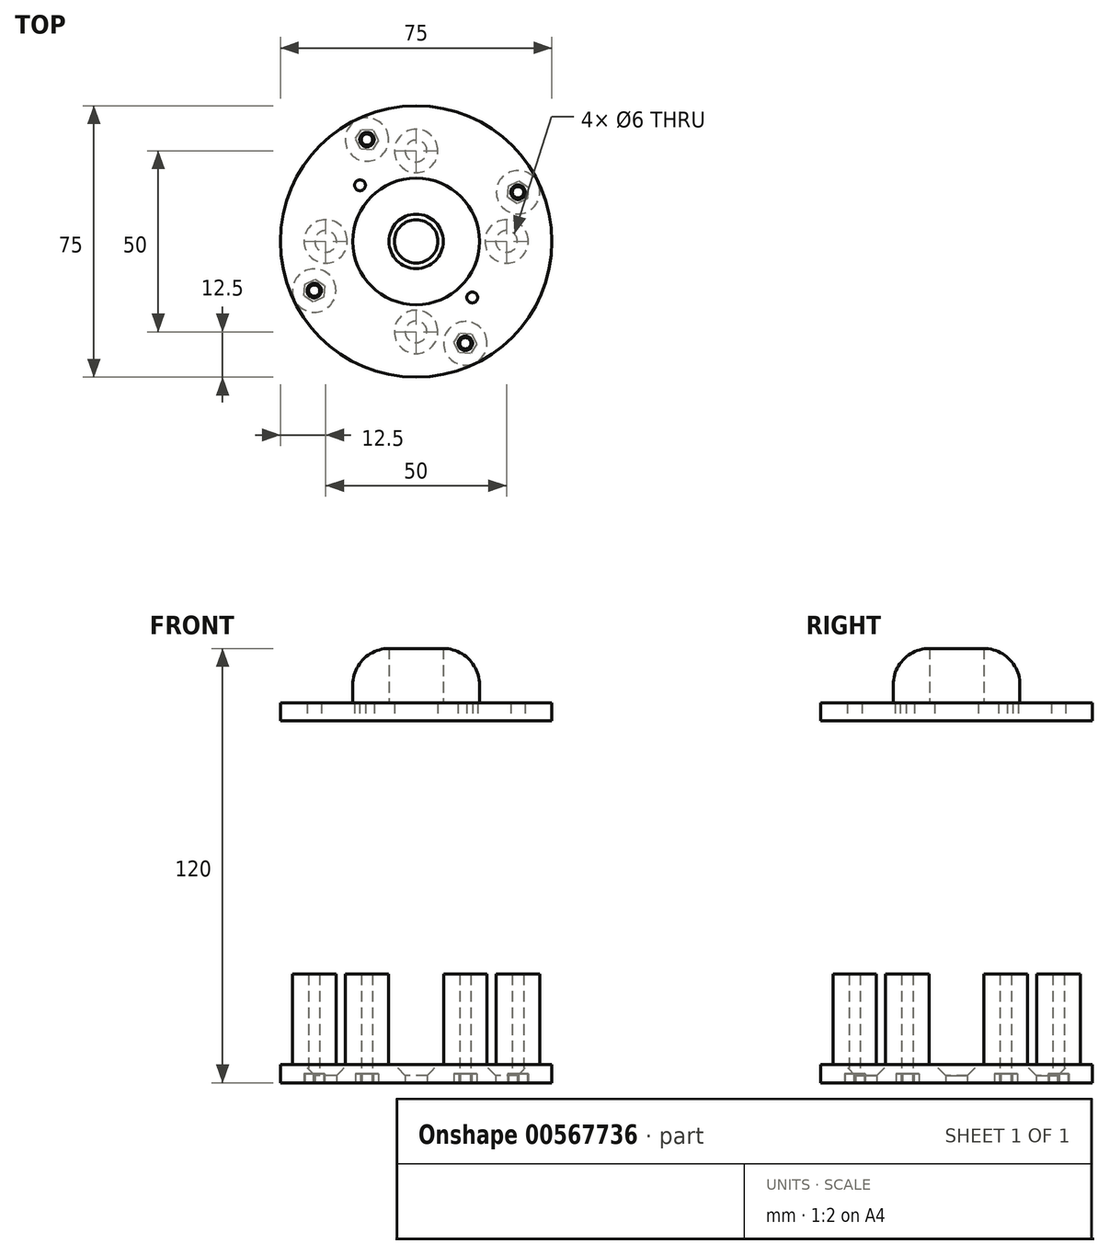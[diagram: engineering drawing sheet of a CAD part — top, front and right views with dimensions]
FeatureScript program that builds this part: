
annotation { "Feature Type Name" : "Feature", "Feature Type Description" : "" }
export const myFeature = defineFeature(function(context is Context, id is Id, definition is map)
    precondition{}
    {
        {
            var Q0;
            Q0=qCreatedBy(makeId("Top.planeOp"),FACE);
            var sketch = newSketch(context, id + "F0", { "sketchPlane" : qUnion([Q0])});
            skCircle(sketch, "E0", {"center": v(0, 0) * mm, "radius": 37.5 * mm});
            skCircle(sketch, "E1", {"center": v(0, 25) * mm, "radius": 3 * mm});
            skCircle(sketch, "E2.1.0", {"center": v(-25, 0) * mm, "radius": 3 * mm});
            skCircle(sketch, "E2.2.0", {"center": v(0, -25) * mm, "radius": 3 * mm});
            skCircle(sketch, "E2.3.0", {"center": v(25, 0) * mm, "radius": 3 * mm});
            skCircle(sketch, "E3.cCircle", {"center": v(28.15, 13.59) * mm, "radius": 2.75 * mm, "construction": true});
            skLineSegment(sketch, "E3.0", {"start": v(30.78, 11.8) * mm, "end": v(27.92, 10.42) * mm});
            skLineSegment(sketch, "E3.1", {"start": v(27.92, 10.42) * mm, "end": v(25.3, 12.2) * mm});
            skLineSegment(sketch, "E3.2", {"start": v(25.3, 12.2) * mm, "end": v(25.52, 15.38) * mm});
            skLineSegment(sketch, "E3.3", {"start": v(25.52, 15.38) * mm, "end": v(28.38, 16.76) * mm});
            skLineSegment(sketch, "E3.4", {"start": v(28.38, 16.76) * mm, "end": v(31, 14.97) * mm});
            skLineSegment(sketch, "E3.5", {"start": v(31, 14.97) * mm, "end": v(30.78, 11.8) * mm});
            skPoint(sketch, "E3.0.midPoint", {"position": v(29.35, 11.11) * mm});
            skLineSegment(sketch, "E4", {"start": v(0, 0) * mm, "end": v(0, 57.37) * mm, "construction": true});
            skLineSegment(sketch, "E5", {"start": v(0, 0) * mm, "end": v(83.24, 0) * mm, "construction": true});
            skLineSegment(sketch, "E6", {"start": v(0, 0) * mm, "end": v(43.66, 21.08) * mm, "construction": true});
            skLineSegment(sketch, "E7.1.0", {"start": v(-16.76, 28.38) * mm, "end": v(-14.97, 31) * mm});
            skLineSegment(sketch, "E7.1.1", {"start": v(-15.38, 25.52) * mm, "end": v(-16.76, 28.38) * mm});
            skLineSegment(sketch, "E7.1.2", {"start": v(-12.2, 25.3) * mm, "end": v(-15.38, 25.52) * mm});
            skLineSegment(sketch, "E7.1.3", {"start": v(-10.42, 27.92) * mm, "end": v(-12.2, 25.3) * mm});
            skLineSegment(sketch, "E7.1.4", {"start": v(-11.8, 30.78) * mm, "end": v(-10.42, 27.92) * mm});
            skLineSegment(sketch, "E7.1.5", {"start": v(-14.97, 31) * mm, "end": v(-11.8, 30.78) * mm});
            skLineSegment(sketch, "E7.2.0", {"start": v(-28.38, -16.76) * mm, "end": v(-31, -14.97) * mm});
            skLineSegment(sketch, "E7.2.1", {"start": v(-25.52, -15.38) * mm, "end": v(-28.38, -16.76) * mm});
            skLineSegment(sketch, "E7.2.2", {"start": v(-25.3, -12.2) * mm, "end": v(-25.52, -15.38) * mm});
            skLineSegment(sketch, "E7.2.3", {"start": v(-27.92, -10.42) * mm, "end": v(-25.3, -12.2) * mm});
            skLineSegment(sketch, "E7.2.4", {"start": v(-30.78, -11.8) * mm, "end": v(-27.92, -10.42) * mm});
            skLineSegment(sketch, "E7.2.5", {"start": v(-31, -14.97) * mm, "end": v(-30.78, -11.8) * mm});
            skLineSegment(sketch, "E7.3.0", {"start": v(16.76, -28.38) * mm, "end": v(14.97, -31) * mm});
            skLineSegment(sketch, "E7.3.1", {"start": v(15.38, -25.52) * mm, "end": v(16.76, -28.38) * mm});
            skLineSegment(sketch, "E7.3.2", {"start": v(12.2, -25.3) * mm, "end": v(15.38, -25.52) * mm});
            skLineSegment(sketch, "E7.3.3", {"start": v(10.42, -27.92) * mm, "end": v(12.2, -25.3) * mm});
            skLineSegment(sketch, "E7.3.4", {"start": v(11.8, -30.78) * mm, "end": v(10.42, -27.92) * mm});
            skLineSegment(sketch, "E7.3.5", {"start": v(14.97, -31) * mm, "end": v(11.8, -30.78) * mm});
            skCircle(sketch, "E8", {"center": v(28.15, 13.59) * mm, "radius": 1.55 * mm});
            skCircle(sketch, "E9.1.0", {"center": v(-13.59, 28.15) * mm, "radius": 1.55 * mm});
            skCircle(sketch, "E9.2.0", {"center": v(-28.15, -13.59) * mm, "radius": 1.55 * mm});
            skCircle(sketch, "E9.3.0", {"center": v(13.59, -28.15) * mm, "radius": 1.55 * mm});
            skLineSegment(sketch, "E10.bottom", {"start": v(-21.15, -21.15) * mm, "end": v(21.15, -21.15) * mm, "construction": true});
            skLineSegment(sketch, "E10.top", {"start": v(-21.15, 21.15) * mm, "end": v(21.15, 21.15) * mm, "construction": true});
            skLineSegment(sketch, "E10.left", {"start": v(-21.15, -21.15) * mm, "end": v(-21.15, 21.15) * mm, "construction": true});
            skLineSegment(sketch, "E10.right", {"start": v(21.15, -21.15) * mm, "end": v(21.15, 21.15) * mm, "construction": true});
            skCircle(sketch, "E11", {"center": v(28.15, 13.59) * mm, "radius": 6 * mm});
            skCircle(sketch, "E12.1.0", {"center": v(-13.59, 28.15) * mm, "radius": 6 * mm});
            skCircle(sketch, "E12.2.0", {"center": v(-28.15, -13.59) * mm, "radius": 6 * mm});
            skCircle(sketch, "E12.3.0", {"center": v(13.59, -28.15) * mm, "radius": 6 * mm});
            skSolve(sketch);
        }
        {
            var Q0;
            Q0=makeQuery(id+"F0.imprint","IMPRINT",FACE,{"disambiguationData":[TD([[makeQuery(id+"F0.imprint","IMPRINT",EDGE,{"derivedFrom":sQuery(id+"F0.wireOp",EDGE,"E0")}),1.0]])]});
            var Q1;
            Q1=makeQuery(id+"F0.imprint","IMPRINT",FACE,{"disambiguationData":[TD([[makeQuery(id+"F0.imprint","IMPRINT",EDGE,{"derivedFrom":sQuery(id+"F0.wireOp",EDGE,"E7.1.0")}),-1.0]])]});
            var Q2;
            Q2=makeQuery(id+"F0.imprint","IMPRINT",FACE,{"disambiguationData":[TD([[makeQuery(id+"F0.imprint","IMPRINT",EDGE,{"derivedFrom":sQuery(id+"F0.wireOp",EDGE,"E7.3.0")}),-1.0]])]});
            var Q3;
            Q3=makeQuery(id+"F0.imprint","IMPRINT",FACE,{"disambiguationData":[TD([[makeQuery(id+"F0.imprint","IMPRINT",EDGE,{"derivedFrom":sQuery(id+"F0.wireOp",EDGE,"E7.2.0")}),-1.0]])]});
            var Q4;
            Q4=makeQuery(id+"F0.imprint","IMPRINT",FACE,{"disambiguationData":[TD([[makeQuery(id+"F0.imprint","IMPRINT",EDGE,{"derivedFrom":sQuery(id+"F0.wireOp",EDGE,"E3.0")}),1.0]])]});
            var Q5;
            Q5=makeQuery(id+"F0.imprint","IMPRINT",FACE,{"disambiguationData":[TD([[makeQuery(id+"F0.imprint","IMPRINT",EDGE,{"derivedFrom":sQuery(id+"F0.wireOp",EDGE,"E3.0")}),-1.0]])]});
            var Q6;
            Q6=makeQuery(id+"F0.imprint","IMPRINT",FACE,{"disambiguationData":[TD([[makeQuery(id+"F0.imprint","IMPRINT",EDGE,{"derivedFrom":sQuery(id+"F0.wireOp",EDGE,"E7.2.0")}),1.0]])]});
            var Q7;
            Q7=makeQuery(id+"F0.imprint","IMPRINT",FACE,{"disambiguationData":[TD([[makeQuery(id+"F0.imprint","IMPRINT",EDGE,{"derivedFrom":sQuery(id+"F0.wireOp",EDGE,"E7.1.0")}),1.0]])]});
            var Q8;
            Q8=makeQuery(id+"F0.imprint","IMPRINT",FACE,{"disambiguationData":[TD([[makeQuery(id+"F0.imprint","IMPRINT",EDGE,{"derivedFrom":sQuery(id+"F0.wireOp",EDGE,"E7.3.0")}),1.0]])]});
            extrude(context, id + "F1", {"entities" : qUnion([Q0, Q1, Q2, Q3, Q4, Q5, Q6, Q7, Q8]), "depth" : 5 * mm, "offsetDistance" : 25 * mm});
        }
        {
            var Q0;
            Q0=makeQuery(id+"F1.opExtrude","CAP_EDGE",EDGE,{"disambiguationData":[OSD([sQuery(id+"F0.wireOp",EDGE,"E1")])],"isStart":false});
            var Q1;
            Q1=makeQuery(id+"F1.opExtrude","CAP_EDGE",EDGE,{"disambiguationData":[OSD([sQuery(id+"F0.wireOp",EDGE,"E2.3.0")])],"isStart":false});
            var Q2;
            Q2=makeQuery(id+"F1.opExtrude","CAP_EDGE",EDGE,{"disambiguationData":[OSD([sQuery(id+"F0.wireOp",EDGE,"E2.2.0")])],"isStart":false});
            var Q3;
            Q3=makeQuery(id+"F1.opExtrude","CAP_EDGE",EDGE,{"disambiguationData":[OSD([sQuery(id+"F0.wireOp",EDGE,"E2.1.0")])],"isStart":false});
            chamfer(context, id + "F2", {"entities" : qUnion([Q0, Q1, Q2, Q3]), "width" : 3 * mm, "tangentPropagation" : true});
        }
        {
            var Q0;
            Q0=qCreatedBy(makeId("Top.planeOp"),FACE);
            cPlane(context, id + "F3", {"entities" : qUnion([Q0]), "cplaneType" : CPlaneType.OFFSET, "offset" : 100 * mm, "width" : 150 * mm, "height" : 150 * mm});
        }
        {
            var Q0;
            Q0=qCreatedBy(id+"F3.planeOp",FACE);
            var sketch = newSketch(context, id + "F4", { "sketchPlane" : qUnion([Q0])});
            skCircle(sketch, "E13", {"center": v(0, 0) * mm, "radius": 37.5 * mm});
            skCircle(sketch, "E14", {"center": v(28.15, 13.59) * mm, "radius": 2 * mm});
            skCircle(sketch, "E15.1.0", {"center": v(-13.59, 28.15) * mm, "radius": 2 * mm});
            skCircle(sketch, "E15.2.0", {"center": v(-28.15, -13.59) * mm, "radius": 2 * mm});
            skCircle(sketch, "E15.3.0", {"center": v(13.59, -28.15) * mm, "radius": 2 * mm});
            skLineSegment(sketch, "E16.bottom", {"start": v(21.15, 21.15) * mm, "end": v(-21.15, 21.15) * mm, "construction": true});
            skLineSegment(sketch, "E16.top", {"start": v(21.15, -21.15) * mm, "end": v(-21.15, -21.15) * mm, "construction": true});
            skLineSegment(sketch, "E16.left", {"start": v(21.15, 21.15) * mm, "end": v(21.15, -21.15) * mm, "construction": true});
            skLineSegment(sketch, "E16.right", {"start": v(-21.15, 21.15) * mm, "end": v(-21.15, -21.15) * mm, "construction": true});
            skLineSegment(sketch, "E17", {"start": v(0, 0) * mm, "end": v(0, -15.5) * mm});
            skLineSegment(sketch, "E18", {"start": v(0, -15.5) * mm, "end": v(15.5, -15.5) * mm});
            skCircle(sketch, "E19", {"center": v(15.5, -15.5) * mm, "radius": 1.5 * mm});
            skCircle(sketch, "E20.MirrorC", {"center": v(-15.5, -15.5) * mm, "radius": 1.5 * mm});
            skLineSegment(sketch, "E21", {"start": v(0, 0) * mm, "end": v(8.71, 0) * mm, "construction": true});
            skCircle(sketch, "E22.MirrorC", {"center": v(-15.5, 15.5) * mm, "radius": 1.5 * mm});
            skCircle(sketch, "E23.MirrorC", {"center": v(15.5, 15.5) * mm, "radius": 1.5 * mm});
            skCircle(sketch, "E24", {"center": v(0, 0) * mm, "radius": 6 * mm});
            skSolve(sketch);
        }
        {
            var Q0;
            Q0=makeQuery(id+"F4.imprint","IMPRINT",FACE,{"disambiguationData":[TD([[makeQuery(id+"F4.imprint","IMPRINT",EDGE,{"derivedFrom":sQuery(id+"F4.wireOp",EDGE,"E13")}),1.0]])]});
            var Q1;
            Q1=makeQuery(id+"F4.imprint","IMPRINT",FACE,{"disambiguationData":[TD([[makeQuery(id+"F4.imprint","IMPRINT",EDGE,{"derivedFrom":sQuery(id+"F4.wireOp",EDGE,"E19")}),-1.0]])]});
            extrude(context, id + "F5", {"entities" : qUnion([Q0, Q1]), "depth" : 5 * mm, "offsetDistance" : 25 * mm});
        }
        {
            var Q0;
            Q0=makeQuery(id+"F4.imprint","IMPRINT",FACE,{"disambiguationData":[TD([[makeQuery(id+"F4.imprint","IMPRINT",EDGE,{"derivedFrom":sQuery(id+"F4.wireOp",EDGE,"E19")}),-1.0]])]});
            var Q1;
            Q1=makeQuery(id+"F4.imprint","IMPRINT",FACE,{"disambiguationData":[TD([[makeQuery(id+"F4.imprint","IMPRINT",EDGE,{"derivedFrom":sQuery(id+"F4.wireOp",EDGE,"E20.MirrorC")}),1.0]])]});
            var Q2;
            Q2=makeQuery(id+"F4.imprint","IMPRINT",FACE,{"disambiguationData":[TD([[makeQuery(id+"F4.imprint","IMPRINT",EDGE,{"derivedFrom":sQuery(id+"F4.wireOp",EDGE,"E22.MirrorC")}),-1.0]])]});
            var Q3;
            Q3=makeQuery(id+"F4.imprint","IMPRINT",FACE,{"disambiguationData":[TD([[makeQuery(id+"F4.imprint","IMPRINT",EDGE,{"derivedFrom":sQuery(id+"F4.wireOp",EDGE,"E23.MirrorC")}),1.0]])]});
            extrude(context, id + "F6", {"entities" : qUnion([Q0, Q1, Q2, Q3]), "depth" : 5 * mm, "offsetDistance" : 25 * mm});
        }
        {
            var Q0;
            Q0=makeQuery(id+"F0.imprint","IMPRINT",FACE,{"disambiguationData":[TD([[makeQuery(id+"F0.imprint","IMPRINT",EDGE,{"derivedFrom":sQuery(id+"F0.wireOp",EDGE,"E3.0")}),1.0]])]});
            var Q1;
            Q1=makeQuery(id+"F0.imprint","IMPRINT",FACE,{"disambiguationData":[TD([[makeQuery(id+"F0.imprint","IMPRINT",EDGE,{"derivedFrom":sQuery(id+"F0.wireOp",EDGE,"E3.0")}),-1.0]])]});
            var Q2;
            Q2=makeQuery(id+"F0.imprint","IMPRINT",FACE,{"disambiguationData":[TD([[makeQuery(id+"F0.imprint","IMPRINT",EDGE,{"derivedFrom":sQuery(id+"F0.wireOp",EDGE,"E7.1.0")}),1.0]])]});
            var Q3;
            Q3=makeQuery(id+"F0.imprint","IMPRINT",FACE,{"disambiguationData":[TD([[makeQuery(id+"F0.imprint","IMPRINT",EDGE,{"derivedFrom":sQuery(id+"F0.wireOp",EDGE,"E7.1.0")}),-1.0]])]});
            var Q4;
            Q4=makeQuery(id+"F0.imprint","IMPRINT",FACE,{"disambiguationData":[TD([[makeQuery(id+"F0.imprint","IMPRINT",EDGE,{"derivedFrom":sQuery(id+"F0.wireOp",EDGE,"E7.2.0")}),1.0]])]});
            var Q5;
            Q5=makeQuery(id+"F0.imprint","IMPRINT",FACE,{"disambiguationData":[TD([[makeQuery(id+"F0.imprint","IMPRINT",EDGE,{"derivedFrom":sQuery(id+"F0.wireOp",EDGE,"E7.2.0")}),-1.0]])]});
            var Q6;
            Q6=makeQuery(id+"F0.imprint","IMPRINT",FACE,{"disambiguationData":[TD([[makeQuery(id+"F0.imprint","IMPRINT",EDGE,{"derivedFrom":sQuery(id+"F0.wireOp",EDGE,"E7.3.0")}),1.0]])]});
            var Q7;
            Q7=makeQuery(id+"F0.imprint","IMPRINT",FACE,{"disambiguationData":[TD([[makeQuery(id+"F0.imprint","IMPRINT",EDGE,{"derivedFrom":sQuery(id+"F0.wireOp",EDGE,"E7.3.0")}),-1.0]])]});
            extrude(context, id + "F7", {"entities" : qUnion([Q0, Q1, Q2, Q3, Q4, Q5, Q6, Q7]), "operationType" : NewBodyOperationType.ADD, "depth" : 30 * mm, "offsetDistance" : 25 * mm});
        }
        {
            var Q0;
            Q0=makeQuery(id+"F0.imprint","IMPRINT",FACE,{"disambiguationData":[TD([[makeQuery(id+"F0.imprint","IMPRINT",EDGE,{"derivedFrom":sQuery(id+"F0.wireOp",EDGE,"E7.2.0")}),-1.0]])]});
            var Q1;
            Q1=makeQuery(id+"F0.imprint","IMPRINT",FACE,{"disambiguationData":[TD([[makeQuery(id+"F0.imprint","IMPRINT",EDGE,{"derivedFrom":sQuery(id+"F0.wireOp",EDGE,"E7.1.0")}),-1.0]])]});
            var Q2;
            Q2=makeQuery(id+"F0.imprint","IMPRINT",FACE,{"disambiguationData":[TD([[makeQuery(id+"F0.imprint","IMPRINT",EDGE,{"derivedFrom":sQuery(id+"F0.wireOp",EDGE,"E3.0")}),-1.0]])]});
            var Q3;
            Q3=makeQuery(id+"F0.imprint","IMPRINT",FACE,{"disambiguationData":[TD([[makeQuery(id+"F0.imprint","IMPRINT",EDGE,{"derivedFrom":sQuery(id+"F0.wireOp",EDGE,"E7.3.0")}),-1.0]])]});
            extrude(context, id + "F8", {"entities" : qUnion([Q0, Q1, Q2, Q3]), "operationType" : NewBodyOperationType.REMOVE, "depth" : 2.5 * mm, "offsetDistance" : 25 * mm});
        }
        {
            var Q0;
            Q0=makeQuery(id+"F6.opExtrude","CAP_EDGE",EDGE,{"disambiguationData":[OSD([sQuery(id+"F4.wireOp",EDGE,"E15.2.0")])],"isStart":false});
            var Q1;
            Q1=makeQuery(id+"F6.opExtrude","CAP_EDGE",EDGE,{"disambiguationData":[OSD([sQuery(id+"F4.wireOp",EDGE,"E15.1.0")])],"isStart":false});
            var Q2;
            Q2=makeQuery(id+"F6.opExtrude","CAP_EDGE",EDGE,{"disambiguationData":[OSD([sQuery(id+"F4.wireOp",EDGE,"E14")])],"isStart":false});
            var Q3;
            Q3=makeQuery(id+"F6.opExtrude","CAP_EDGE",EDGE,{"disambiguationData":[OSD([sQuery(id+"F4.wireOp",EDGE,"E15.3.0")])],"isStart":false});
            chamfer(context, id + "F9", {"entities" : qUnion([Q0, Q1, Q2, Q3]), "width" : 3 * mm, "tangentPropagation" : true});
        }
        {
            var Q0;
            Q0=makeQuery(id+"F6.opExtrude","CAP_FACE",FACE,{"disambiguationData":[OSD([sQuery(id+"F4.wireOp",EDGE,"E13"),sQuery(id+"F4.wireOp",EDGE,"E14"),sQuery(id+"F4.wireOp",EDGE,"E15.1.0"),sQuery(id+"F4.wireOp",EDGE,"E15.2.0"),sQuery(id+"F4.wireOp",EDGE,"E15.3.0"),sQuery(id+"F4.wireOp",EDGE,"E19"),sQuery(id+"F4.wireOp",EDGE,"E20.MirrorC"),sQuery(id+"F4.wireOp",EDGE,"E22.MirrorC"),sQuery(id+"F4.wireOp",EDGE,"E23.MirrorC")])],"isStart":false});
            var sketch = newSketch(context, id + "F10", { "sketchPlane" : qUnion([Q0])});
            skCircle(sketch, "E25", {"center": v(0, 0) * mm, "radius": 17.5 * mm});
            skCircle(sketch, "E26", {"center": v(0, 0) * mm, "radius": 7.5 * mm});
            skSolve(sketch);
        }
        {
            var Q0;
            Q0=makeQuery(id+"F10.imprint","IMPRINT",FACE,{"disambiguationData":[TD([[makeQuery(id+"F10.imprint","IMPRINT",EDGE,{"derivedFrom":sQuery(id+"F10.wireOp",EDGE,"E25")}),1.0]])]});
            extrude(context, id + "F11", {"entities" : qUnion([Q0]), "operationType" : NewBodyOperationType.ADD, "depth" : 15 * mm, "offsetDistance" : 25 * mm});
        }
        {
            var Q0;
            Q0=makeQuery(id+"F11.opExtrude","CAP_EDGE",EDGE,{"disambiguationData":[OSD([sQuery(id+"F10.wireOp",EDGE,"E25")])],"isStart":false});
            fillet(context, id + "F12", {"entities" : qUnion([Q0]), "radius" : 10 * mm, "tangentPropagation" : true, "allowEdgeOverflow" : false});
        }
    });
